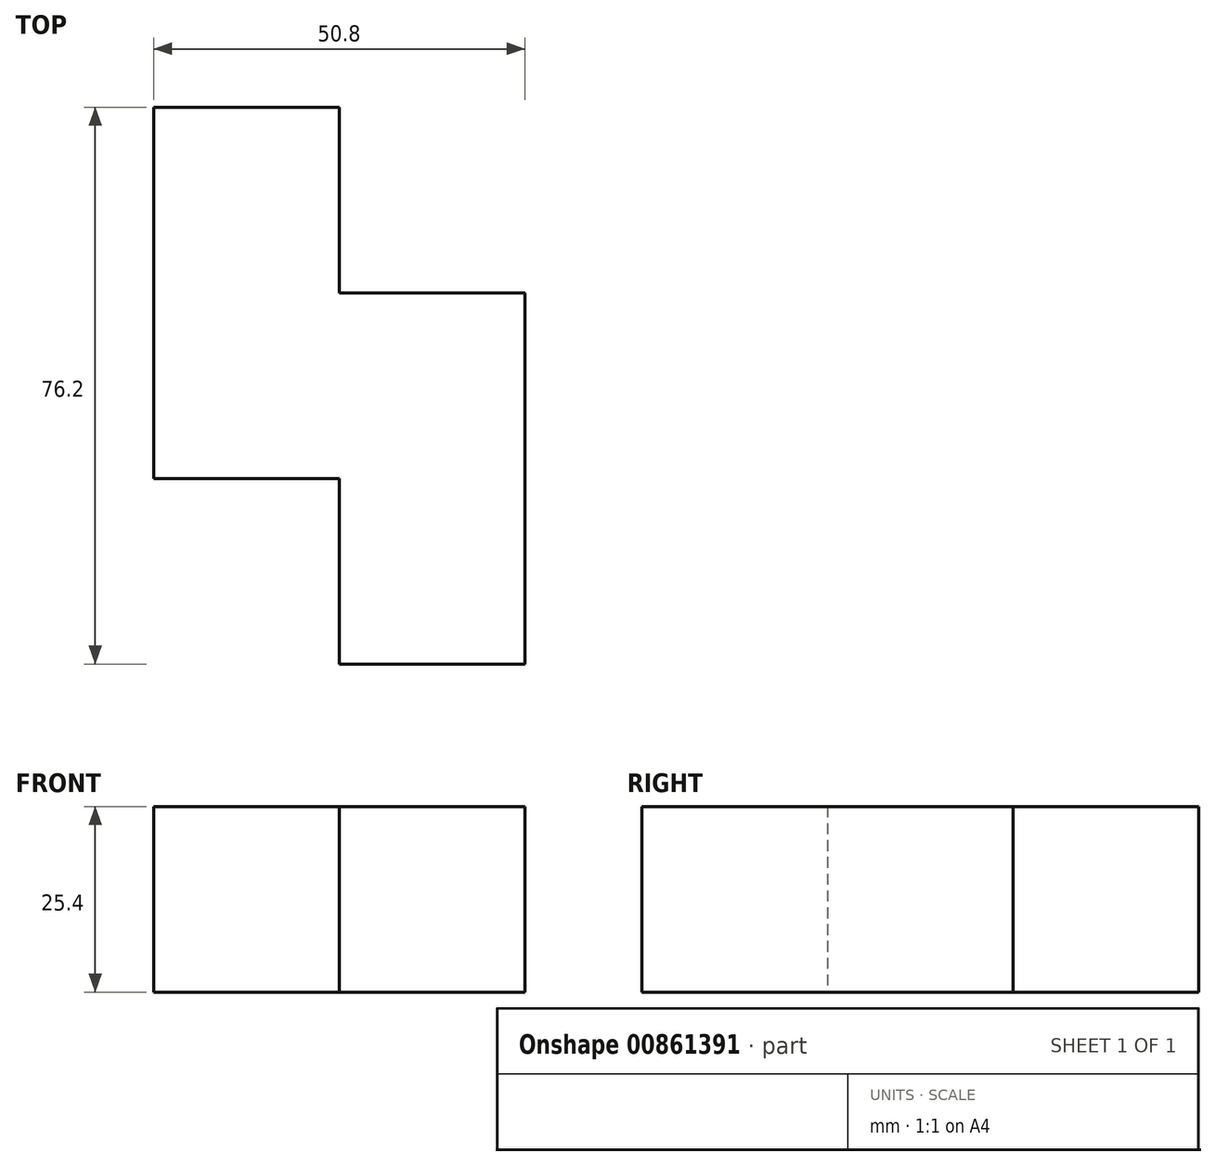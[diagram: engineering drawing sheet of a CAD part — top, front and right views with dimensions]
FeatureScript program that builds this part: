
annotation { "Feature Type Name" : "Feature", "Feature Type Description" : "" }
export const myFeature = defineFeature(function(context is Context, id is Id, definition is map)
    precondition{}
    {
        {
            var Q0;
            Q0=qCreatedBy(makeId("Top.planeOp"),FACE);
            var sketch = newSketch(context, id + "F0", { "sketchPlane" : qUnion([Q0])});
            skLineSegment(sketch, "E0.bottom", {"start": v(12.7, -25.4) * mm, "end": v(-12.7, -25.4) * mm});
            skLineSegment(sketch, "E0.top", {"start": v(12.7, 25.4) * mm, "end": v(-12.7, 25.4) * mm});
            skLineSegment(sketch, "E0.left", {"start": v(12.7, 0) * mm, "end": v(12.7, 25.4) * mm});
            skLineSegment(sketch, "E0.right", {"start": v(-12.7, -25.4) * mm, "end": v(-12.7, 25.4) * mm});
            skPoint(sketch, "E0.middle", {"position": v(0, 0) * mm});
            skLineSegment(sketch, "E1.bottom", {"start": v(12.7, 0) * mm, "end": v(38.1, 0) * mm});
            skLineSegment(sketch, "E1.top", {"start": v(12.7, -50.8) * mm, "end": v(38.1, -50.8) * mm});
            skLineSegment(sketch, "E1.left", {"start": v(12.7, -25.4) * mm, "end": v(12.7, -50.8) * mm});
            skLineSegment(sketch, "E1.right", {"start": v(38.1, 0) * mm, "end": v(38.1, -50.8) * mm});
            skSolve(sketch);
        }
        {
            var Q0;
            Q0 = qSketchRegion(id + "F0", true);
            extrude(context, id + "F1", {"entities" : qUnion([Q0]), "depth" : 25.4 * mm, "offsetDistance" : 25.4 * mm});
        }
    });
